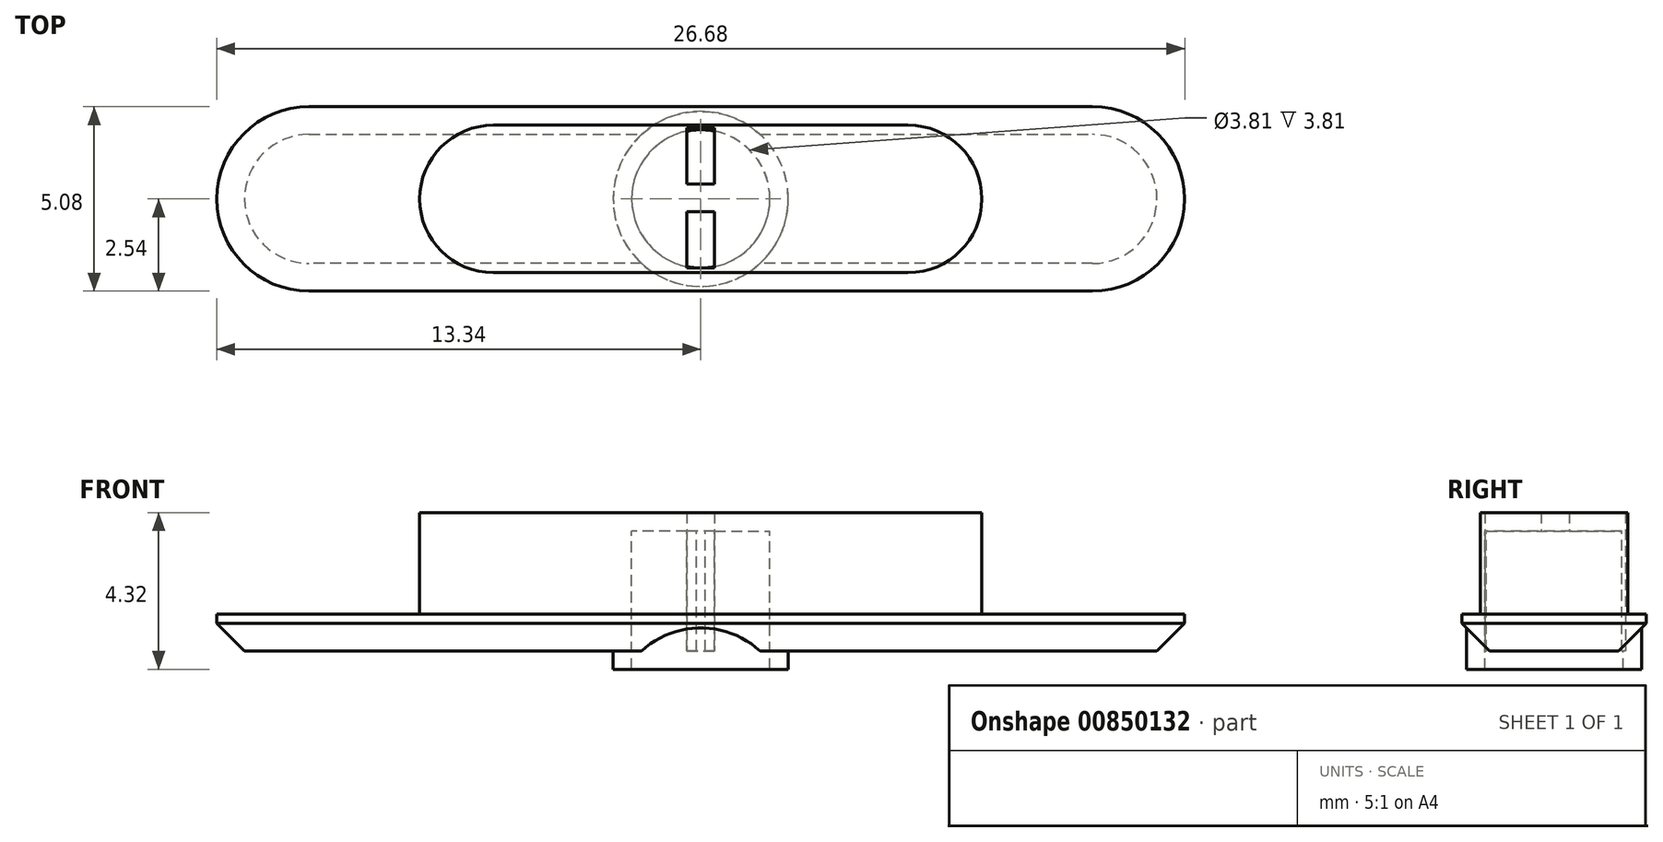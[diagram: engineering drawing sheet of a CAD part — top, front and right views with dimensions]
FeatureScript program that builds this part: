
annotation { "Feature Type Name" : "Feature", "Feature Type Description" : "" }
export const myFeature = defineFeature(function(context is Context, id is Id, definition is map)
    precondition{}
    {
        {
            var Q0;
            Q0=qCreatedBy(makeId("Top.planeOp"),FACE);
            var sketch = newSketch(context, id + "F0", { "sketchPlane" : qUnion([Q0])});
            skLineSegment(sketch, "E0.bottom", {"start": v(-10.8, 2.54) * mm, "end": v(10.8, 2.54) * mm});
            skLineSegment(sketch, "E0.top", {"start": v(-10.8, -2.54) * mm, "end": v(10.8, -2.54) * mm});
            skLineSegment(sketch, "E0.left", {"start": v(-13.34, 0) * mm, "end": v(-13.34, 0) * mm});
            skLineSegment(sketch, "E0.right", {"start": v(13.34, 0) * mm, "end": v(13.34, 0) * mm});
            skPoint(sketch, "E1", {"position": v(0, -2.54) * mm});
            skPoint(sketch, "E2", {"position": v(13.34, 0) * mm});
            skPoint(sketch, "E3.visualSharp", {"position": v(-13.34, 2.54) * mm});
            skArc(sketch, "E3.filletArc", {"start": v(-10.8, 2.54) * mm, "mid": v(-12.6, 1.8) * mm, "end": v(-13.33, 0) * mm});
            skPoint(sketch, "E4.visualSharp", {"position": v(-13.34, -2.54) * mm});
            skArc(sketch, "E4.filletArc", {"start": v(-13.34, 0) * mm, "mid": v(-12.6, -1.8) * mm, "end": v(-10.8, -2.54) * mm});
            skPoint(sketch, "E5.visualSharp", {"position": v(13.34, -2.54) * mm});
            skArc(sketch, "E5.filletArc", {"start": v(10.8, -2.54) * mm, "mid": v(12.6, -1.8) * mm, "end": v(13.34, 0) * mm});
            skPoint(sketch, "E6.visualSharp", {"position": v(13.34, 2.54) * mm});
            skArc(sketch, "E6.filletArc", {"start": v(13.34, 0) * mm, "mid": v(12.6, 1.8) * mm, "end": v(10.8, 2.54) * mm});
            skSolve(sketch);
        }
        {
            var Q0;
            Q0=makeQuery(id+"F0.imprint","IMPRINT",FACE,{"disambiguationData":[TD([[makeQuery(id+"F0.imprint","IMPRINT",EDGE,{"derivedFrom":sQuery(id+"F0.wireOp",EDGE,"E0.bottom")}),-1.0]])]});
            extrude(context, id + "F1", {"entities" : qUnion([Q0]), "depth" : 1.02 * mm, "offsetDistance" : 25.4 * mm});
        }
        {
            var Q0;
            Q0=qCreatedBy(makeId("Top.planeOp"),FACE);
            var sketch = newSketch(context, id + "F2", { "sketchPlane" : qUnion([Q0])});
            skLineSegment(sketch, "E7.bottom", {"start": v(-5.72, 2.03) * mm, "end": v(5.72, 2.03) * mm});
            skLineSegment(sketch, "E7.top", {"start": v(-5.71, -2.03) * mm, "end": v(5.72, -2.03) * mm});
            skLineSegment(sketch, "E7.left", {"start": v(-7.75, 0) * mm, "end": v(-7.75, 0) * mm});
            skLineSegment(sketch, "E7.right", {"start": v(7.75, 0) * mm, "end": v(7.75, 0) * mm});
            skPoint(sketch, "E8", {"position": v(0, -2.03) * mm});
            skPoint(sketch, "E9", {"position": v(7.75, 0) * mm});
            skPoint(sketch, "E10.visualSharp", {"position": v(-7.75, 2.03) * mm});
            skArc(sketch, "E10.filletArc", {"start": v(-5.72, 2.03) * mm, "mid": v(-7.15, 1.44) * mm, "end": v(-7.75, 0) * mm});
            skPoint(sketch, "E11.visualSharp", {"position": v(-7.75, -2.03) * mm});
            skArc(sketch, "E11.filletArc", {"start": v(-7.75, 0) * mm, "mid": v(-7.15, -1.44) * mm, "end": v(-5.71, -2.03) * mm});
            skPoint(sketch, "E12.visualSharp", {"position": v(7.75, -2.03) * mm});
            skArc(sketch, "E12.filletArc", {"start": v(5.72, -2.03) * mm, "mid": v(7.15, -1.44) * mm, "end": v(7.75, 0) * mm});
            skPoint(sketch, "E13.visualSharp", {"position": v(7.75, 2.03) * mm});
            skArc(sketch, "E13.filletArc", {"start": v(7.75, 0) * mm, "mid": v(7.15, 1.44) * mm, "end": v(5.72, 2.03) * mm});
            skSolve(sketch);
        }
        {
            var Q0;
            Q0=makeQuery(id+"F2.imprint","IMPRINT",FACE,{"disambiguationData":[TD([[makeQuery(id+"F2.imprint","IMPRINT",EDGE,{"derivedFrom":sQuery(id+"F2.wireOp",EDGE,"E7.bottom")}),-1.0]])]});
            extrude(context, id + "F3", {"entities" : qUnion([Q0]), "operationType" : NewBodyOperationType.ADD, "depth" : 3.8 * mm, "offsetDistance" : 25.4 * mm});
        }
        {
            var Q0;
            Q0=qCreatedBy(makeId("Top.planeOp"),FACE);
            var sketch = newSketch(context, id + "F4", { "sketchPlane" : qUnion([Q0])});
            skCircle(sketch, "E14", {"center": v(0, 0) * mm, "radius": 1.9 * mm});
            skSolve(sketch);
        }
        {
            var Q0;
            Q0=qCreatedBy(makeId("Top.planeOp"),FACE);
            var Q1;
            Q1=qCreatedBy(makeId("Top.planeOp"),FACE);
            var sketch = newSketch(context, id + "F5", { "sketchPlane" : qUnion([Q0, Q1])});
            skCircle(sketch, "E15", {"center": v(0, 0) * mm, "radius": 1.9 * mm});
            skCircle(sketch, "E16.0", {"center": v(0, 0) * mm, "radius": 2.41 * mm});
            skSolve(sketch);
        }
        {
            var Q0;
            Q0=makeQuery(id+"F5.imprint","IMPRINT",FACE,{"disambiguationData":[TD([[makeQuery(id+"F5.imprint","IMPRINT",EDGE,{"derivedFrom":sQuery(id+"F5.wireOp",EDGE,"E15")}),-1.0]])]});
            extrude(context, id + "F6", {"entities" : qUnion([Q0]), "operationType" : NewBodyOperationType.ADD, "depth" : -0.5 * mm, "offsetDistance" : 25.4 * mm});
        }
        {
            var Q0;
            Q0 = qSketchRegion(id + "F4", true);
            extrude(context, id + "F7", {"entities" : qUnion([Q0]), "operationType" : NewBodyOperationType.REMOVE, "oppositeDirection" : true, "depth" : -3.3 * mm, "offsetDistance" : 25.4 * mm});
        }
        {
            var Q0;
            Q0=qCreatedBy(makeId("Top.planeOp"),FACE);
            var Q1;
            Q1=qCreatedBy(makeId("Top.planeOp"),FACE);
            var sketch = newSketch(context, id + "F8", { "sketchPlane" : qUnion([Q0, Q1])});
            skLineSegment(sketch, "E17.bottom", {"start": v(-0.38, 1.96) * mm, "end": v(0.38, 1.96) * mm});
            skLineSegment(sketch, "E17.top", {"start": v(-0.38, 0.42) * mm, "end": v(0.38, 0.42) * mm});
            skLineSegment(sketch, "E17.left", {"start": v(-0.38, 1.96) * mm, "end": v(-0.38, 0.42) * mm});
            skLineSegment(sketch, "E17.right", {"start": v(0.38, 1.96) * mm, "end": v(0.38, 0.42) * mm});
            skPoint(sketch, "E18", {"position": v(0, 0.42) * mm});
            skLineSegment(sketch, "E19.bottom", {"start": v(-0.38, -0.35) * mm, "end": v(0.38, -0.35) * mm});
            skLineSegment(sketch, "E19.top", {"start": v(-0.38, -1.9) * mm, "end": v(0.38, -1.9) * mm});
            skLineSegment(sketch, "E19.left", {"start": v(-0.38, -0.35) * mm, "end": v(-0.38, -1.9) * mm});
            skLineSegment(sketch, "E19.right", {"start": v(0.38, -0.35) * mm, "end": v(0.38, -1.9) * mm});
            skPoint(sketch, "E20", {"position": v(0, -0.35) * mm});
            skSolve(sketch);
        }
        {
            var Q0;
            Q0 = qSketchRegion(id + "F8", true);
            extrude(context, id + "F9", {"entities" : qUnion([Q0]), "operationType" : NewBodyOperationType.REMOVE, "oppositeDirection" : true, "depth" : -25.4 * mm, "offsetDistance" : 25.4 * mm});
        }
        {
            var Q0;
            Q0=makeQuery(id+"F1.opExtrude","CAP_EDGE",EDGE,{"disambiguationData":[OSD([sQuery(id+"F0.wireOp",EDGE,"E0.top")])],"isStart":true});
            chamfer(context, id + "F10", {"entities" : qUnion([Q0]), "width" : 0.76 * mm, "tangentPropagation" : true});
        }
    });
